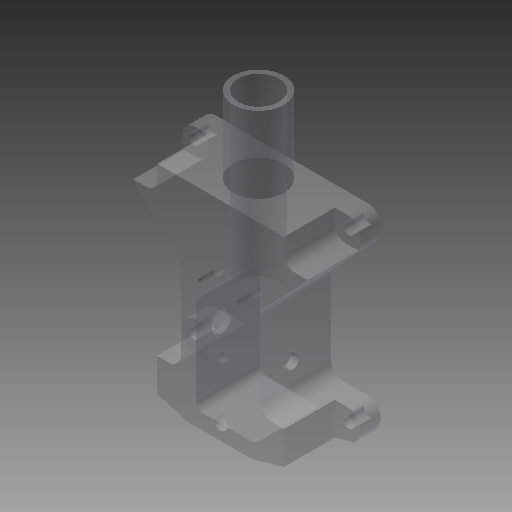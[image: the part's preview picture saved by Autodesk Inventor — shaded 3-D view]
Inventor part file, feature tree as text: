
AUTODESK INVENTOR PART (.ipt)
format: ipt  version: 2018 (Build 220112000, 112)  size: 313,856 bytes
history: native  units: mm
features: extrude x11, reference x10, sketch x3, projected_geometry x2, fillet x1, hole x1
ambient origin geometry x8: Origin, YZ Plane, XZ Plane, XY Plane, X Axis, Y Axis, Z Axis, Center Point
bodies: Solid1 (feature_tree)
feature tree (28):
  extrude  "Extrusion1"  Depth=25.0mm
  extrude  "Extrusion2"  Depth=22.5mm
  extrude  "Extrusion3"  Depth=25.0mm TaperAngle=0.0deg
  extrude  "Extrusion4"  Depth=1.0mm
  fillet  "Rundung1"  Radius=16.0mm
  extrude  "Extrusion5"  Depth=20.0mm
  extrude  "Extrusion6"  Depth=1.0mm
  extrude  "Extrusion7"  Depth=1.0mm
  extrude  "Extrusion8"  Depth=30.0mm TaperAngle=0.0deg
  extrude  "Extrusion9"  Depth=30.0mm TaperAngle=0.0deg
  hole  "Bohrung1"  [1 undecoded]
  extrude  "Extrusion10"  Depth=30.0mm TaperAngle=0.0deg
  extrude  "Extrusion11"  Depth=3.0mm
  sketch  "Skizze1"  dims[d0=28.0mm d1=0.0mm d2=25.0mm]
  reference  "Referenz1"
  reference  "Referenz2"
  projected_geometry  "Projizierte Kontur1"
  reference  "Referenz3"
  reference  "Referenz4"
  reference  "Referenz5"
  reference  "Referenz6"
  reference  "Referenz7"
  reference  "Referenz8"
  reference  "Referenz9"
  sketch  "Skizze8"  dims[d3=40.0mm d5=22.5mm]
  projected_geometry  "Projizierte Kontur2"
  sketch  "Skizze9"  dims[d6=5.0mm d7=25.0mm d8=0.0mm d9=15.0mm d10=16.0mm d11=20.0mm d12=15.0mm d13=35.0mm d14=30.0mm d15=0.0mm d16=30.0mm d17=0.0mm d18=3.0mm d19=30.0mm d20=0.0mm d21=3.0mm d22=15.0mm d23=12.5mm d24=30.0mm d25=0.0mm d26=1.5mm d27=4.9mm d28=10.0mm d29=30.0mm d30=0.0mm d47=0.0mm d48=3.0mm d49=35.0mm d50=5.0mm d51=5.0mm d52=3.0mm d53=30.0mm d54=5.0mm d55=5.0mm d56=30.0mm d57=0.0mm d58=5.0mm d59=12.5mm d60=3.0mm d65=20.0mm d66=0.0mm d67=10.0mm d68=10.0mm d69=4.0mm d70=10.0mm d71=10.0mm d72=4.0mm d73=10.0mm d74=10.0mm d75=2.459mm d76=6.0mm d77=4.0mm d78=2.0mm d79=90.0deg d80=8.0mm d81=20.594885mm d82=8.0mm d84=3.0mm d85=0.0mm d86=10.0mm d87=1.0mm d88=0.0mm]
  reference  "Referenz10"
note: 1 required parameter value undecoded (feature->parameter linkage not recoverable at this tier; creation-order binding heuristic only, values carry confidence <= 0.55)
